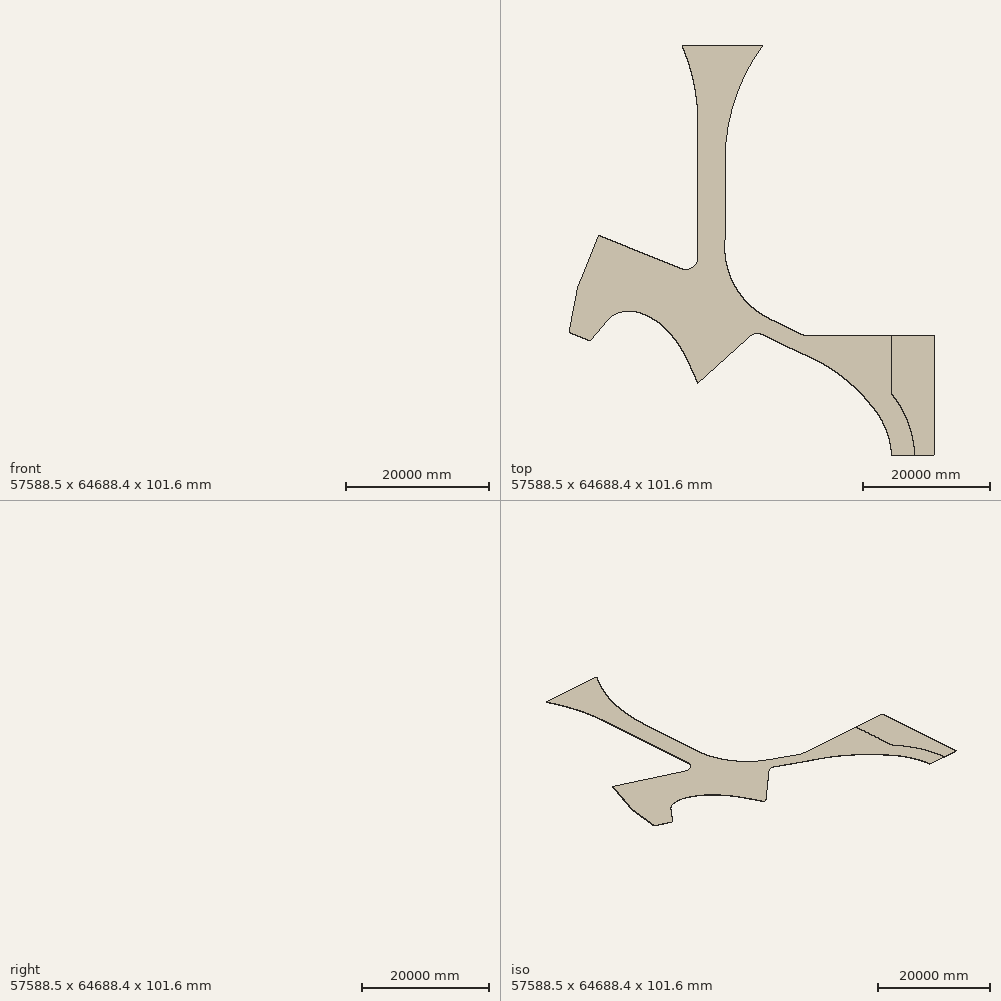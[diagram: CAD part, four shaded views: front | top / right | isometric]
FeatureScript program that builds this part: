
annotation { "Feature Type Name" : "Feature", "Feature Type Description" : "" }
export const myFeature = defineFeature(function(context is Context, id is Id, definition is map)
    precondition{}
    {
        {
            var Q0;
            Q0=qCreatedBy(makeId("Top.planeOp"),FACE);
            var sketch = newSketch(context, id + "F0", { "sketchPlane" : qUnion([Q0])});
            skLineSegment(sketch, "E0", {"start": v(0, 0) * mm, "end": v(0, 9753.6) * mm});
            skLineSegment(sketch, "E1", {"start": v(0, 0) * mm, "end": v(-3048, 0) * mm});
            skLineSegment(sketch, "E2", {"start": v(0, 9753.6) * mm, "end": v(0, 18897.6) * mm});
            skLineSegment(sketch, "E3", {"start": v(0, 18897.6) * mm, "end": v(-6705.6, 18897.6) * mm});
            skLineSegment(sketch, "E4", {"start": v(-6705.6, 18897.6) * mm, "end": v(-6705.6, 9753.6) * mm});
            skLineSegment(sketch, "E5", {"start": v(-3048, 0) * mm, "end": v(-6705.6, 0) * mm});
            skArc(sketch, "E6", {"start": v(-3048, 0) * mm, "mid": v(-4072.16, 5178.54) * mm, "end": v(-6705.6, 9753.6) * mm});
            skArc(sketch, "E7", {"start": v(-6705.6, 0) * mm, "mid": v(-7515.15, 3949.38) * mm, "end": v(-9534.4, 7438.74) * mm});
            skLineSegment(sketch, "E8", {"start": v(-6705.6, 18897.6) * mm, "end": v(-19841.03, 18897.6) * mm});
            skLineSegment(sketch, "E9", {"start": v(-20944.52, 19149.83) * mm, "end": v(-25912.26, 21545.98) * mm});
            skLineSegment(sketch, "E10", {"start": v(-21613.37, 16426.8) * mm, "end": v(-27104.03, 19075.18) * mm});
            skFitSpline(sketch, "E11", {"points": [v(-9534.4, 7438.74) * mm, v(-12087.31, 10366.2) * mm, v(-15146.34, 12918.9) * mm, v(-18479.62, 14986.38) * mm, v(-21613.37, 16426.8) * mm], "startDerivative": vector(-15040.21, 18988.47) * mm, "endDerivative": vector(-8974.19, 3954.8) * mm});
            skLineSegment(sketch, "E12", {"start": v(-28948.87, 18811.8) * mm, "end": v(-37237.78, 11348.43) * mm});
            skLineSegment(sketch, "E13", {"start": v(-39884.98, 29472.32) * mm, "end": v(-52884.84, 34724.6) * mm});
            skArc(sketch, "E14", {"start": v(-39884.98, 29472.32) * mm, "mid": v(-38086.68, 29661.33) * mm, "end": v(-37237.78, 31257.88) * mm});
            skLineSegment(sketch, "E15.trimOffspring", {"start": v(-37237.78, 31257.88) * mm, "end": v(-37237.78, 52496.44) * mm});
            skLineSegment(sketch, "E16", {"start": v(-52884.84, 34724.6) * mm, "end": v(-56234.12, 26434.84) * mm});
            skLineSegment(sketch, "E17", {"start": v(-56234.12, 26434.84) * mm, "end": v(-57588.54, 19421.1) * mm});
            skLineSegment(sketch, "E18", {"start": v(-57588.54, 19421.1) * mm, "end": v(-54197.27, 18050.94) * mm});
            skFitSpline(sketch, "E19", {"points": [v(-54197.27, 18050.94) * mm, v(-52215.85, 20391.6) * mm, v(-51057.9, 21703.94) * mm, v(-49977.13, 22398.72) * mm, v(-48240.2, 22746.1) * mm, v(-46766.84, 22609.8) * mm, v(-45038.1, 21911.35) * mm, v(-43234.27, 20816.18) * mm, v(-41871.43, 19503.82) * mm, v(-40404.68, 17689.7) * mm, v(-39015.14, 15219.38) * mm, v(-37934.38, 12903.47) * mm, v(-37237.78, 11348.43) * mm], "startDerivative": vector(20609.05, 24131.14) * mm, "endDerivative": vector(8635.42, -19352.58) * mm});
            skArc(sketch, "E20", {"start": v(-27104.03, 19075.18) * mm, "mid": v(-28066.55, 19224.4) * mm, "end": v(-28948.87, 18811.8) * mm});
            skArc(sketch, "E21", {"start": v(-25912.26, 21545.98) * mm, "mid": v(-31395.65, 26683.29) * mm, "end": v(-32970.58, 34030.33) * mm});
            skLineSegment(sketch, "E22", {"start": v(-32970.58, 46400.44) * mm, "end": v(-32970.58, 34030.33) * mm});
            skPoint(sketch, "E23", {"position": v(-39777.78, 64688.44) * mm});
            skPoint(sketch, "E24", {"position": v(-26976.18, 64688.44) * mm});
            skPoint(sketch, "E25", {"position": v(-37237.78, 52496.44) * mm});
            skPoint(sketch, "E26", {"position": v(-32970.58, 46400.44) * mm});
            skArc(sketch, "E27", {"start": v(-37237.78, 52496.44) * mm, "mid": v(-37879.53, 58723.33) * mm, "end": v(-39777.78, 64688.44) * mm});
            skArc(sketch, "E28", {"start": v(-32970.58, 46400.44) * mm, "mid": v(-31433.76, 56023.12) * mm, "end": v(-26976.18, 64688.44) * mm});
            skLineSegment(sketch, "E29", {"start": v(-39777.78, 64688.44) * mm, "end": v(-26976.18, 64688.44) * mm});
            skPoint(sketch, "E30.visualSharp", {"position": v(-20421.6, 18897.6) * mm});
            skArc(sketch, "E30.filletArc", {"start": v(-20944.52, 19149.83) * mm, "mid": v(-20407, 18961.46) * mm, "end": v(-19841.03, 18897.6) * mm});
            skSolve(sketch);
        }
        {
            var Q0;
            Q0=makeQuery(id+"F0.imprint","IMPRINT",FACE,{"disambiguationData":[TD([[makeQuery(id+"F0.imprint","IMPRINT",EDGE,{"derivedFrom":sQuery(id+"F0.wireOp",EDGE,"E4")}),-1.0]])]});
            extrude(context, id + "F1", {"entities" : qUnion([Q0]), "oppositeDirection" : true, "depth" : 50.8 * mm, "offsetDistance" : 25.4 * mm});
        }
        {
            var Q0;
            Q0=makeQuery(id+"F0.imprint","IMPRINT",FACE,{"disambiguationData":[TD([[makeQuery(id+"F0.imprint","IMPRINT",EDGE,{"derivedFrom":sQuery(id+"F0.wireOp",EDGE,"E0")}),1.0]])]});
            extrude(context, id + "F2", {"entities" : qUnion([Q0]), "oppositeDirection" : true, "depth" : 127 * mm, "offsetDistance" : 25.4 * mm});
        }
        {
            var Q0;
            Q0=makeQuery(id+"F2.opExtrude","CAP_FACE",FACE,{"disambiguationData":[OSD([sQuery(id+"F0.wireOp",EDGE,"E0"),sQuery(id+"F0.wireOp",EDGE,"E1"),sQuery(id+"F0.wireOp",EDGE,"E2"),sQuery(id+"F0.wireOp",EDGE,"E3"),sQuery(id+"F0.wireOp",EDGE,"E4"),sQuery(id+"F0.wireOp",EDGE,"E6")])],"isStart":false});
            extrude(context, id + "F3", {"entities" : qUnion([Q0]), "operationType" : NewBodyOperationType.REMOVE, "oppositeDirection" : true, "depth" : 25.4 * mm, "offsetDistance" : 25.4 * mm});
        }
    });
